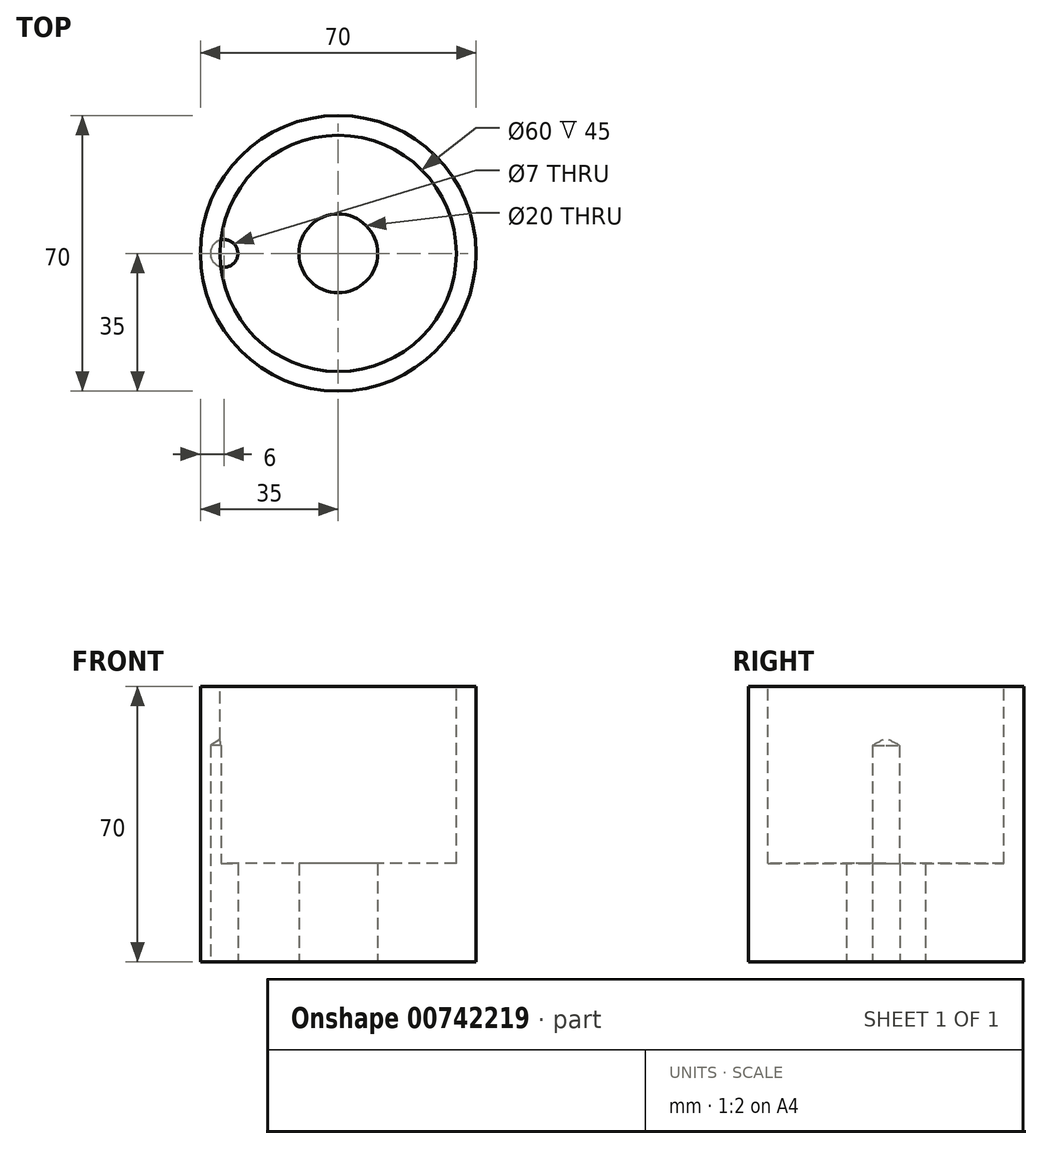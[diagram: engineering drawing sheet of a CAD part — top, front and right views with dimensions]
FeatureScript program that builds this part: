
annotation { "Feature Type Name" : "Feature", "Feature Type Description" : "" }
export const myFeature = defineFeature(function(context is Context, id is Id, definition is map)
    precondition{}
    {
        {
            var Q0;
            Q0=qCreatedBy(makeId("Top.planeOp"),FACE);
            var sketch = newSketch(context, id + "F0", { "sketchPlane" : qUnion([Q0])});
            skCircle(sketch, "E0", {"center": v(0, 0) * mm, "radius": 35 * mm});
            skSolve(sketch);
        }
        {
            var Q0;
            Q0=makeQuery(id+"F0.imprint","IMPRINT",FACE,{"disambiguationData":[TD([[makeQuery(id+"F0.imprint","IMPRINT",EDGE,{"derivedFrom":sQuery(id+"F0.wireOp",EDGE,"E0")}),1.0]])]});
            extrude(context, id + "F1", {"entities" : qUnion([Q0]), "oppositeDirection" : true, "depth" : 70 * mm, "offsetDistance" : 25 * mm});
        }
        {
            var Q0;
            Q0=makeQuery(id+"F1.opExtrude","CAP_FACE",FACE,{"disambiguationData":[OSD([sQuery(id+"F0.wireOp",EDGE,"E0")])],"isStart":true});
            shell(context, id + "F2", {"entities" : qUnion([Q0]), "thickness" : 5 * mm});
        }
        {
            var Q0;
            {var subQ0=sQuery(id+"F0.wireOp",EDGE,"E0");Q0=makeQuery(id+"F2.opShell","OFFSET_FACE",FACE,{"disambiguationData":[OSD([subQ0]),TDD([makeQuery(id+"F1.opExtrude","CAP_FACE",FACE,{"disambiguationData":[OSD([subQ0])],"isStart":false})])]});}
            extrude(context, id + "F3", {"entities" : qUnion([Q0]), "operationType" : NewBodyOperationType.ADD, "depth" : 20 * mm, "offsetDistance" : 25 * mm});
        }
        {
            var Q0;
            Q0=makeQuery(id+"F1.opExtrude","CAP_FACE",FACE,{"disambiguationData":[OSD([sQuery(id+"F0.wireOp",EDGE,"E0")])],"isStart":false});
            var sketch = newSketch(context, id + "F4", { "sketchPlane" : qUnion([Q0])});
            skCircle(sketch, "E1", {"center": v(-29, 0) * mm, "radius": 2.5 * mm});
            skSolve(sketch);
        }
        {
            var Q0;
            Q0=sQuery(id+"F4.wireOp",VERTEX,"E1.center");
            var Q1;
            Q1=makeQuery(id+"F1.opExtrude","SWEPT_BODY",BODY,{"disambiguationData":[OSD([sQuery(id+"F0.wireOp",EDGE,"E0")])]});
            hole(context, id + "F5", {"style" : HoleStyle.SIMPLE, "endStyle" : HoleEndStyle.BLIND, "holeDiameter" : 7 * mm, "majorDiameter" : 5 * mm, "holeDepth" : 55 * mm, "isTappedThrough" : true, "tappedDepth" : 12 * mm, "tapClearance" : 3, "locations" : qUnion([Q0]), "scope" : qUnion([Q1])});
        }
        {
            var Q0;
            Q0=makeQuery(id+"F1.opExtrude","CAP_FACE",FACE,{"disambiguationData":[OSD([sQuery(id+"F0.wireOp",EDGE,"E0")])],"isStart":false});
            var sketch = newSketch(context, id + "F6", { "sketchPlane" : qUnion([Q0])});
            skCircle(sketch, "E2", {"center": v(0, 0) * mm, "radius": 10 * mm});
            skSolve(sketch);
        }
        {
            var Q0;
            Q0=makeQuery(id+"F6.imprint","IMPRINT",FACE,{"disambiguationData":[TD([[makeQuery(id+"F6.imprint","IMPRINT",EDGE,{"derivedFrom":sQuery(id+"F6.wireOp",EDGE,"E2")}),1.0]])]});
            extrude(context, id + "F7", {"entities" : qUnion([Q0]), "operationType" : NewBodyOperationType.REMOVE, "endBound" : BoundingType.UP_TO_NEXT, "oppositeDirection" : true, "depth" : 25 * mm, "offsetDistance" : 25 * mm});
        }
    });
